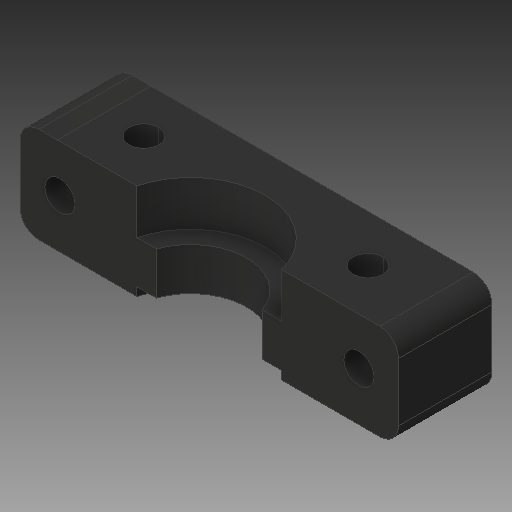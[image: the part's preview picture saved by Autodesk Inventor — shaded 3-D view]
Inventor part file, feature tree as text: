
AUTODESK INVENTOR PART (.ipt)
format: ipt  version: 2017 (Build 210142000, 142)  size: 194,048 bytes
history: native  units: mm
features: sketch x9, other x3
ambient origin geometry x8: Origin, YZ Plane, XZ Plane, XY Plane, X Axis, Y Axis, Z Axis, Center Point
bodies: Solid1 (feature_tree)
feature tree (12):
  other  "Hotend Clamp P2_MIR.ipt"
  other  "Solid1::Hotend Clamp P2_MIR.ipt"
  other  "TaggingFeature1"
  sketch  "Sketch1"  dims[d0=10.0mm]
  sketch  "Sketch2"
  sketch  "Sketch3"
  sketch  "Sketch4"
  sketch  "Sketch5"
  sketch  "Sketch6"
  sketch  "Sketch7"
  sketch  "Sketch8"
  sketch  "Sketch9"
